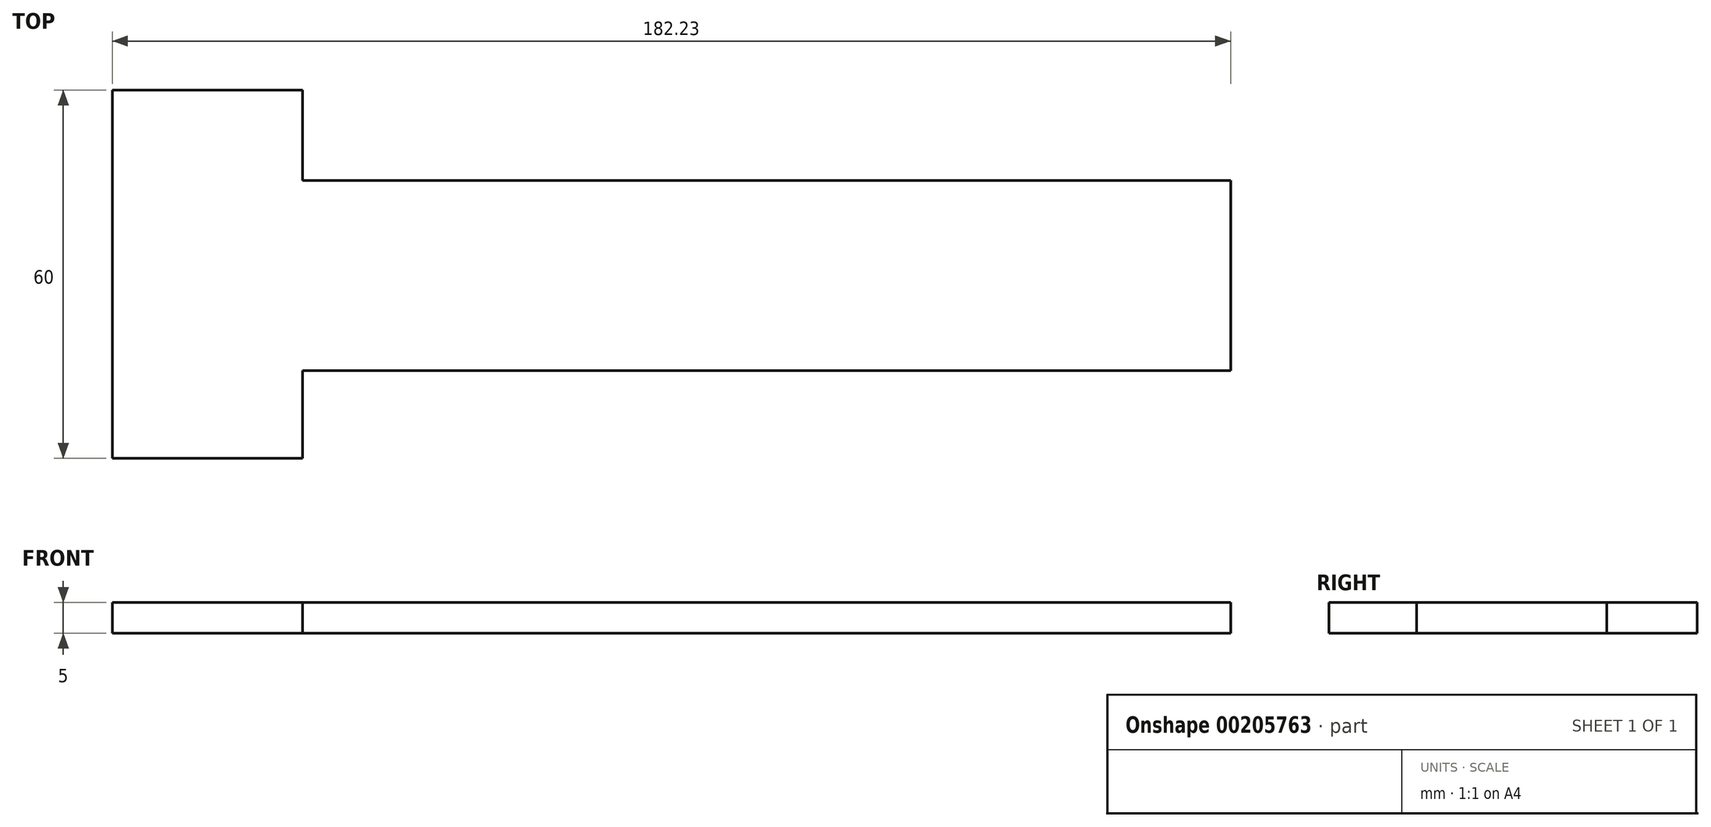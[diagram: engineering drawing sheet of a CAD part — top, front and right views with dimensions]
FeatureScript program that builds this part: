
annotation { "Feature Type Name" : "Feature", "Feature Type Description" : "" }
export const myFeature = defineFeature(function(context is Context, id is Id, definition is map)
    precondition{}
    {
        {
            var Q0;
            Q0=qCreatedBy(makeId("Top.planeOp"),FACE);
            var sketch = newSketch(context, id + "F0", { "sketchPlane" : qUnion([Q0])});
            skLineSegment(sketch, "E0.bottom", {"start": v(-111.18, 23.2) * mm, "end": v(68.82, 23.2) * mm});
            skLineSegment(sketch, "E0.top", {"start": v(-111.18, -7.8) * mm, "end": v(68.82, -7.8) * mm});
            skLineSegment(sketch, "E0.left", {"start": v(-111.18, 23.2) * mm, "end": v(-111.18, -7.8) * mm});
            skLineSegment(sketch, "E0.right", {"start": v(68.82, 23.2) * mm, "end": v(68.82, -7.8) * mm});
            skSolve(sketch);
        }
        {
            var Q0;
            Q0 = qSketchRegion(id + "F0", true);
            extrude(context, id + "F1", {"entities" : qUnion([Q0]), "endBound" : BoundingType.SYMMETRIC, "oppositeDirection" : true, "depth" : 5 * mm});
        }
        {
            var Q0;
            Q0=qCreatedBy(makeId("Top.planeOp"),FACE);
            var sketch = newSketch(context, id + "F2", { "sketchPlane" : qUnion([Q0])});
            skLineSegment(sketch, "E1.bottom", {"start": v(-82.41, -22.09) * mm, "end": v(-113.41, -22.09) * mm});
            skLineSegment(sketch, "E1.top", {"start": v(-82.41, 37.91) * mm, "end": v(-113.41, 37.91) * mm});
            skLineSegment(sketch, "E1.left", {"start": v(-82.41, -22.09) * mm, "end": v(-82.41, 37.91) * mm});
            skLineSegment(sketch, "E1.right", {"start": v(-113.41, -22.09) * mm, "end": v(-113.41, 37.91) * mm});
            skSolve(sketch);
        }
        {
            var Q0;
            Q0=makeQuery(id+"F2.imprint","IMPRINT",FACE,{"disambiguationData":[TD([[makeQuery(id+"F2.imprint","IMPRINT",EDGE,{"derivedFrom":sQuery(id+"F2.wireOp",EDGE,"E1.bottom")}),-1.0]])]});
            extrude(context, id + "F3", {"entities" : qUnion([Q0]), "operationType" : NewBodyOperationType.ADD, "endBound" : BoundingType.SYMMETRIC, "depth" : 5 * mm});
        }
    });
